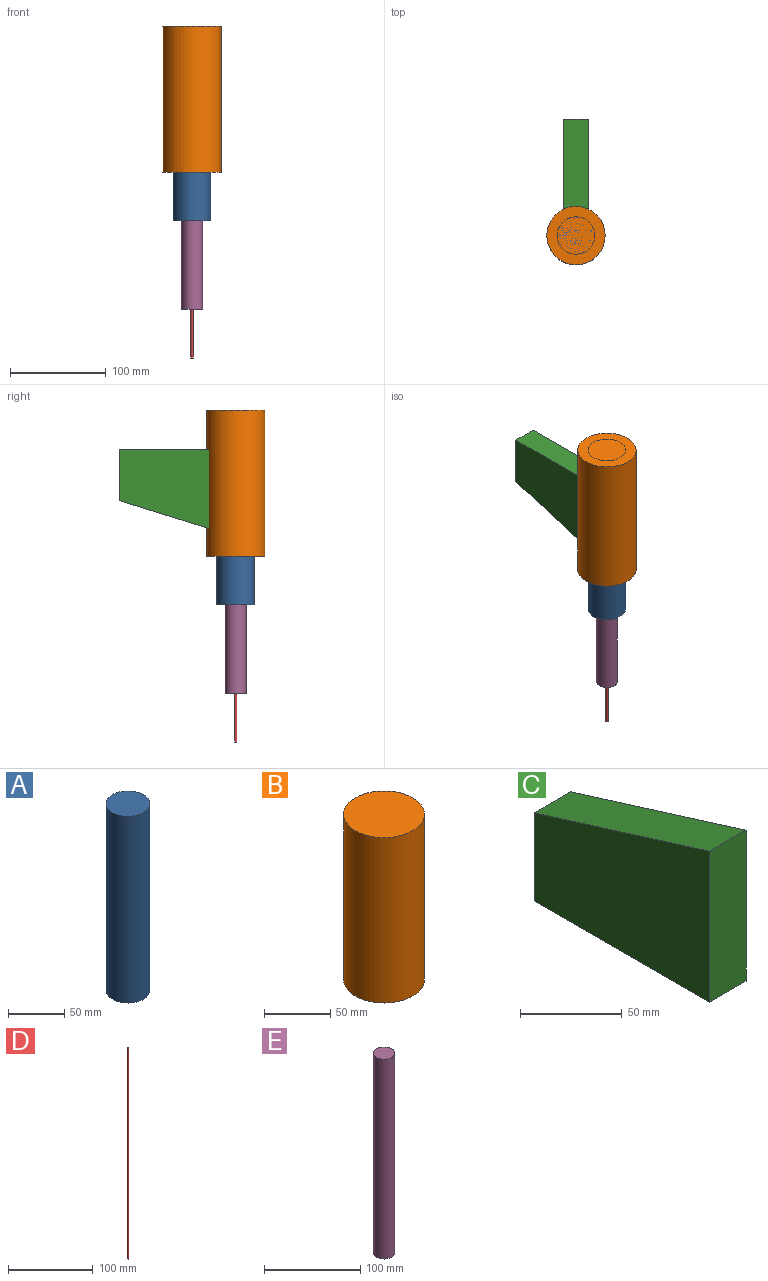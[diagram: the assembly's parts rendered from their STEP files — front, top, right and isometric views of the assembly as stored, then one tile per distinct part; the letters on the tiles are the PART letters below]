
ASSEMBLY  parts=5 mates=5
PART A: 3 faces, bbox 39x39x203.2 mm
  f0: cylinder r=19.51mm len=203.2mm, axis (0,0,-1), area 24915.2mm2, adj f1,f2
  f1: plane 39.03x39.03mm, normal (0,0,1), area 1196.4mm2, adj f0
  f2: plane 39.03x39.03mm, normal (0,0,-1), area 1196.4mm2, adj f0
PART B: 3 faces, bbox 60.9x60.9x152.4 mm
  f0: cylinder r=30.44mm len=152.4mm, axis (0,0,-1), area 29151.2mm2, adj f1,f2
  f1: plane 60.89x60.89mm, normal (0,0,1), area 2911.6mm2, adj f0
  f2: plane 60.89x60.89mm, normal (0,0,-1), area 2911.6mm2, adj f0
PART C: 6 faces, bbox 25.4x121.6x90.6 mm
  f0: plane 121.63x37.76mm, normal (0,0.3,0.96), area 3234.7mm2, adj f1,f3,f4,f5
  f1: plane 90.64x25.4mm, normal (0,-1,0), area 2302.2mm2, adj f0,f2,f4,f5
  f2: plane 121.63x25.4mm, normal (0,0,-1), area 3089.3mm2, adj f1,f3,f4,f5
  f3: plane 52.88x25.4mm, normal (0,1,0), area 1343.2mm2, adj f0,f2,f4,f5
  f4: plane 121.63x90.64mm, normal (1,0,0), area 8727.8mm2, adj f0,f1,f2,f3
  f5: plane 121.63x90.64mm, normal (-1,0,0), area 8727.8mm2, adj f0,f1,f2,f3
PART D: 3 faces, bbox 2.3x2.3x304.8 mm
  f0: cylinder r=1.15mm len=304.8mm, axis (0,0,-1), area 2196.2mm2, adj f1,f2
  f1: plane 2.29x2.29mm, normal (0,0,1), area 4.1mm2, adj f0
  f2: plane 2.29x2.29mm, normal (0,0,-1), area 4.1mm2, adj f0
PART E: 3 faces, bbox 22.1x22.1x254 mm
  f0: cylinder r=11.04mm len=254mm, axis (0,0,-1), area 17613.7mm2, adj f1,f2
  f1: plane 22.07x22.07mm, normal (0,0,1), area 382.7mm2, adj f0
  f2: plane 22.07x22.07mm, normal (0,0,-1), area 382.7mm2, adj f0
PLACE A t=(-71.21,-102.94,92.55)mm
PLACE B t=(-23.82,-48.53,143.35)mm
PLACE C rot(axis=(0,1,0),180deg) t=(-11.12,8,213.49)mm
PLACE D t=(24.03,1.02,-50.8)mm
PLACE E t=(-70.08,0,0)mm
MATE pin_slot E.f0 <-> C.f2  axis (0,0,1) through (-23.82,-48.53,254)mm
MATE pin_slot D.f0 <-> E.f0  axis (0,0,1) through (-23.82,-48.53,254)mm
MATE cylindrical A.f0 <-> E.f0  axis (0,0,1) through (-23.82,-48.53,295.75)mm
MATE cylindrical B.f0 <-> E.f0  axis (0,0,1) through (-23.82,-48.53,295.75)mm
MATE cylindrical D.f0 <-> B.f0  axis (0,0,1) through (-23.82,-48.53,254)mm
